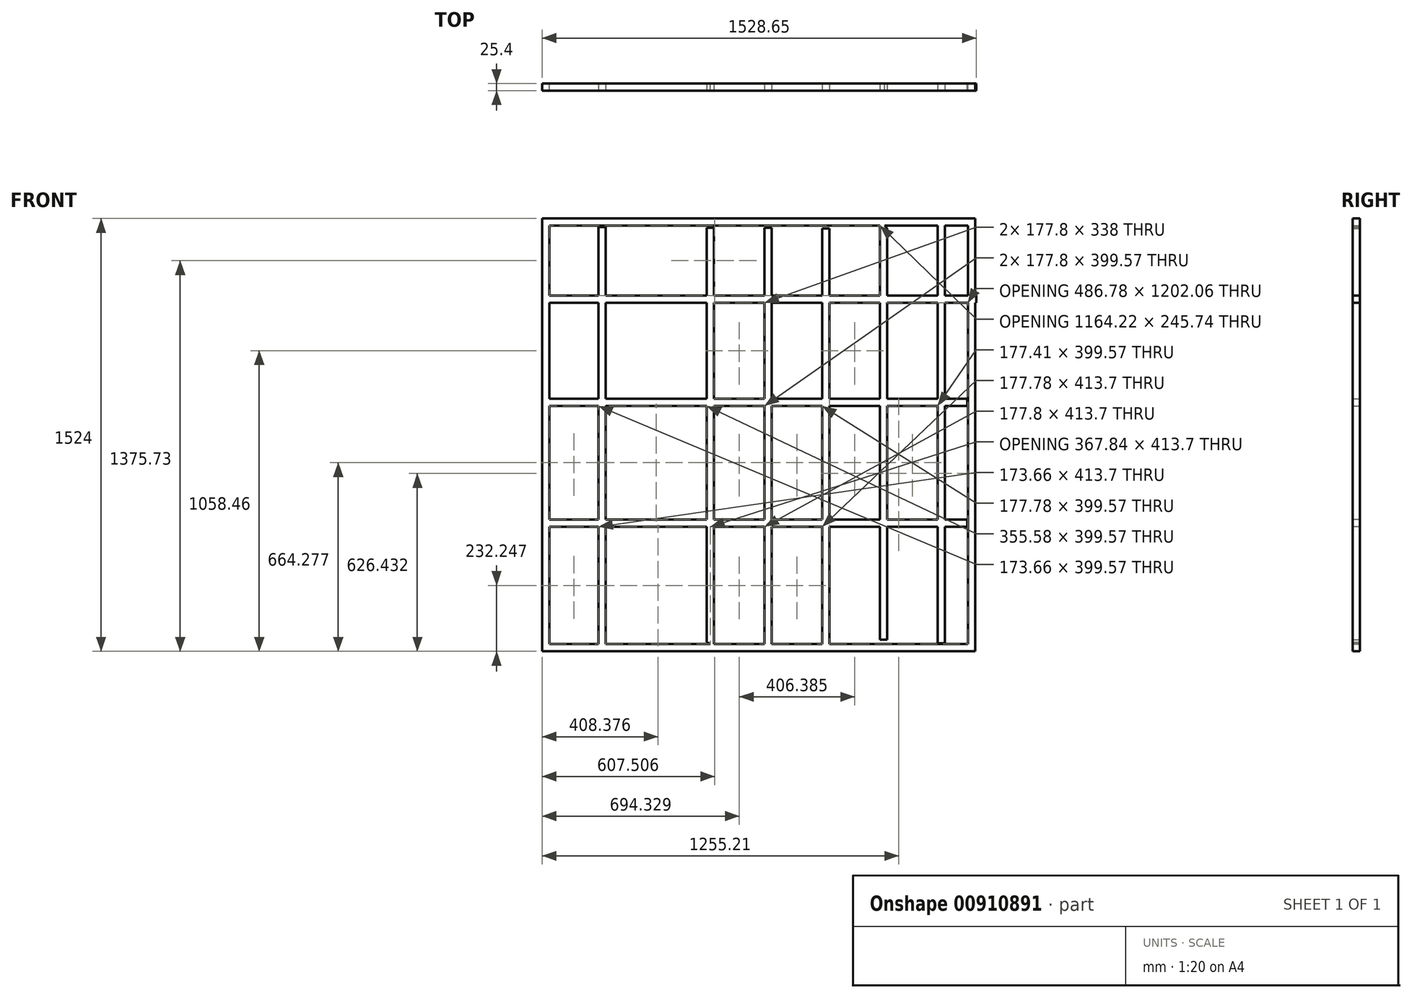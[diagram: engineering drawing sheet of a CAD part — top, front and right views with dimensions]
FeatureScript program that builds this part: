
annotation { "Feature Type Name" : "Feature", "Feature Type Description" : "" }
export const myFeature = defineFeature(function(context is Context, id is Id, definition is map)
    precondition{}
    {
        {
            var Q0;
            Q0=qCreatedBy(makeId("Front.planeOp"),FACE);
            var sketch = newSketch(context, id + "F0", { "sketchPlane" : qUnion([Q0])});
            skLineSegment(sketch, "E0.bottom", {"start": v(-795.6, -653.31) * mm, "end": v(728.4, -653.31) * mm});
            skLineSegment(sketch, "E0.top", {"start": v(-795.6, 870.69) * mm, "end": v(728.4, 870.69) * mm});
            skLineSegment(sketch, "E0.left", {"start": v(-795.6, -653.31) * mm, "end": v(-795.6, 870.69) * mm});
            skLineSegment(sketch, "E0.right", {"start": v(728.4, -653.31) * mm, "end": v(728.4, 870.69) * mm});
            skLineSegment(sketch, "E1.0", {"start": v(-770.2, -627.91) * mm, "end": v(-770.2, 845.29) * mm});
            skLineSegment(sketch, "E1.1", {"start": v(-770.2, -627.91) * mm, "end": v(703, -627.91) * mm});
            skLineSegment(sketch, "E1.2", {"start": v(703, -627.91) * mm, "end": v(703, 845.29) * mm});
            skLineSegment(sketch, "E1.3", {"start": v(-770.2, 845.29) * mm, "end": v(703, 845.29) * mm});
            skSolve(sketch);
        }
        {
            var Q0;
            Q0=makeQuery(id+"F0.imprint","IMPRINT",FACE,{"disambiguationData":[TD([[makeQuery(id+"F0.imprint","IMPRINT",EDGE,{"derivedFrom":sQuery(id+"F0.wireOp",EDGE,"E0.bottom")}),1.0]])]});
            extrude(context, id + "F1", {"entities" : qUnion([Q0]), "depth" : 25.4 * mm, "offsetDistance" : 25.4 * mm});
        }
        {
            var Q0;
            Q0=qCreatedBy(makeId("Front.planeOp"),FACE);
            var sketch = newSketch(context, id + "F2", { "sketchPlane" : qUnion([Q0])});
            skLineSegment(sketch, "E2", {"start": v(-571.14, 841.34) * mm, "end": v(-571.14, -631.86) * mm});
            skLineSegment(sketch, "E3.0", {"start": v(-596.54, 841.34) * mm, "end": v(-596.54, -631.86) * mm});
            skPoint(sketch, "E4", {"position": v(-393.36, 838.36) * mm});
            skPoint(sketch, "E5", {"position": v(-190.16, 838.36) * mm});
            skPoint(sketch, "E6", {"position": v(13.04, 838.36) * mm});
            skPoint(sketch, "E7", {"position": v(216.22, 835.87) * mm});
            skPoint(sketch, "E8", {"position": v(419.42, 835.87) * mm});
            skPoint(sketch, "E9", {"position": v(622.24, 848.4) * mm});
            skLineSegment(sketch, "E10", {"start": v(-393.36, 838.36) * mm, "end": v(-393.36, -634.84) * mm});
            skLineSegment(sketch, "E11", {"start": v(-393.36, -634.84) * mm, "end": v(-393.36, 838.36) * mm});
            skLineSegment(sketch, "E12", {"start": v(-190.16, 838.36) * mm, "end": v(-190.16, -634.84) * mm});
            skLineSegment(sketch, "E13", {"start": v(13.04, 838.36) * mm, "end": v(13.04, -630.6) * mm});
            skLineSegment(sketch, "E14", {"start": v(216.22, 835.87) * mm, "end": v(216.22, -630.6) * mm});
            skLineSegment(sketch, "E15", {"start": v(419.42, 835.87) * mm, "end": v(419.42, -612.28) * mm});
            skLineSegment(sketch, "E16", {"start": v(622.24, 848.4) * mm, "end": v(622.24, -624.5) * mm});
            skLineSegment(sketch, "E17.0", {"start": v(-367.96, -621.44) * mm, "end": v(-367.96, 851.76) * mm});
            skLineSegment(sketch, "E18.0", {"start": v(-215.56, 838.36) * mm, "end": v(-215.56, -621.44) * mm});
            skLineSegment(sketch, "E19.0", {"start": v(-12.36, 838.36) * mm, "end": v(-12.36, -630.6) * mm});
            skLineSegment(sketch, "E20.0", {"start": v(190.82, 835.87) * mm, "end": v(190.82, -630.6) * mm});
            skLineSegment(sketch, "E21.0", {"start": v(394.02, 860.92) * mm, "end": v(394.02, -612.28) * mm});
            skLineSegment(sketch, "E22.0", {"start": v(596.84, 848.4) * mm, "end": v(596.84, -624.5) * mm});
            skLineSegment(sketch, "E23", {"start": v(-596.54, 841.34) * mm, "end": v(-571.14, 841.34) * mm});
            skLineSegment(sketch, "E24", {"start": v(-596.54, -631.86) * mm, "end": v(-571.14, -631.86) * mm});
            skLineSegment(sketch, "E25", {"start": v(-393.36, -634.84) * mm, "end": v(-367.96, -621.44) * mm});
            skLineSegment(sketch, "E26", {"start": v(-393.36, 838.36) * mm, "end": v(-367.96, 851.76) * mm});
            skLineSegment(sketch, "E27", {"start": v(-215.56, 838.36) * mm, "end": v(-190.16, 838.36) * mm});
            skLineSegment(sketch, "E28", {"start": v(-215.56, -621.44) * mm, "end": v(-190.16, -634.84) * mm});
            skLineSegment(sketch, "E29", {"start": v(-12.36, -630.6) * mm, "end": v(13.04, -630.6) * mm});
            skLineSegment(sketch, "E30", {"start": v(-12.36, 838.36) * mm, "end": v(13.04, 838.36) * mm});
            skLineSegment(sketch, "E31", {"start": v(190.82, 835.87) * mm, "end": v(216.22, 835.87) * mm});
            skLineSegment(sketch, "E32", {"start": v(190.82, -630.6) * mm, "end": v(216.22, -630.6) * mm});
            skLineSegment(sketch, "E33", {"start": v(394.02, -612.28) * mm, "end": v(419.42, -612.28) * mm});
            skLineSegment(sketch, "E34", {"start": v(394.02, 860.92) * mm, "end": v(419.42, 835.87) * mm});
            skLineSegment(sketch, "E35", {"start": v(596.84, 848.4) * mm, "end": v(622.24, 848.4) * mm});
            skLineSegment(sketch, "E36", {"start": v(622.24, -624.5) * mm, "end": v(596.84, -624.5) * mm});
            skSolve(sketch);
        }
        {
            var Q0;
            Q0=makeQuery(id+"F2.imprint","IMPRINT",FACE,{"disambiguationData":[TD([[makeQuery(id+"F2.imprint","IMPRINT",EDGE,{"derivedFrom":sQuery(id+"F2.wireOp",EDGE,"E2")}),-1.0]])]});
            var Q1;
            Q1=makeQuery(id+"F2.imprint","IMPRINT",FACE,{"disambiguationData":[TD([[makeQuery(id+"F2.imprint","IMPRINT",EDGE,{"derivedFrom":sQuery(id+"F2.wireOp",EDGE,"E11")}),-1.0]])]});
            var Q2;
            Q2=makeQuery(id+"F2.imprint","IMPRINT",FACE,{"disambiguationData":[TD([[makeQuery(id+"F2.imprint","IMPRINT",EDGE,{"derivedFrom":sQuery(id+"F2.wireOp",EDGE,"E12")}),-1.0]])]});
            var Q3;
            Q3=makeQuery(id+"F2.imprint","IMPRINT",FACE,{"disambiguationData":[TD([[makeQuery(id+"F2.imprint","IMPRINT",EDGE,{"derivedFrom":sQuery(id+"F2.wireOp",EDGE,"E13")}),-1.0]])]});
            var Q4;
            Q4=makeQuery(id+"F2.imprint","IMPRINT",FACE,{"disambiguationData":[TD([[makeQuery(id+"F2.imprint","IMPRINT",EDGE,{"derivedFrom":sQuery(id+"F2.wireOp",EDGE,"E14")}),-1.0]])]});
            var Q5;
            Q5=makeQuery(id+"F2.imprint","IMPRINT",FACE,{"disambiguationData":[TD([[makeQuery(id+"F2.imprint","IMPRINT",EDGE,{"derivedFrom":sQuery(id+"F2.wireOp",EDGE,"E15")}),-1.0]])]});
            var Q6;
            Q6=makeQuery(id+"F2.imprint","IMPRINT",FACE,{"disambiguationData":[TD([[makeQuery(id+"F2.imprint","IMPRINT",EDGE,{"derivedFrom":sQuery(id+"F2.wireOp",EDGE,"E16")}),-1.0]])]});
            extrude(context, id + "F3", {"entities" : qUnion([Q0, Q1, Q2, Q3, Q4, Q5, Q6]), "operationType" : NewBodyOperationType.ADD, "depth" : 25.4 * mm, "offsetDistance" : 25.4 * mm});
        }
        {
            var Q0;
            Q0=qCreatedBy(makeId("Front.planeOp"),FACE);
            var sketch = newSketch(context, id + "F4", { "sketchPlane" : qUnion([Q0])});
            skLineSegment(sketch, "E37", {"start": v(-770.36, 236.15) * mm, "end": v(701.58, 236.15) * mm});
            skLineSegment(sketch, "E38", {"start": v(701.58, -214.22) * mm, "end": v(-770.36, -214.22) * mm});
            skLineSegment(sketch, "E39", {"start": v(-770.36, 599.55) * mm, "end": v(733.06, 599.55) * mm});
            skLineSegment(sketch, "E40.0", {"start": v(-770.36, 574.15) * mm, "end": v(733.06, 574.15) * mm});
            skLineSegment(sketch, "E41.0", {"start": v(-770.36, 210.75) * mm, "end": v(701.58, 210.75) * mm});
            skLineSegment(sketch, "E42.0", {"start": v(701.58, -188.82) * mm, "end": v(-770.36, -188.82) * mm});
            skLineSegment(sketch, "E43", {"start": v(-770.36, 574.15) * mm, "end": v(-770.36, 599.55) * mm});
            skLineSegment(sketch, "E44", {"start": v(-770.36, 236.15) * mm, "end": v(-770.36, 210.75) * mm});
            skLineSegment(sketch, "E45", {"start": v(-770.36, -188.82) * mm, "end": v(-770.36, -214.22) * mm});
            skLineSegment(sketch, "E46", {"start": v(733.06, 599.55) * mm, "end": v(733.06, 574.15) * mm});
            skLineSegment(sketch, "E47", {"start": v(701.58, 236.15) * mm, "end": v(701.58, 210.75) * mm});
            skLineSegment(sketch, "E48", {"start": v(701.58, -214.22) * mm, "end": v(701.58, -188.82) * mm});
            skSolve(sketch);
        }
        {
            var Q0;
            Q0 = qSketchRegion(id + "F4", true);
            extrude(context, id + "F5", {"entities" : qUnion([Q0]), "operationType" : NewBodyOperationType.ADD, "depth" : 25.4 * mm, "offsetDistance" : 25.4 * mm});
        }
    });
